# Revit family: Gas Ace 220_250_LOD-5
name_source: partatom
category: Mechanical Equipment
revit_build: Autodesk Revit 2015 (Build: 20160512_1515(x64)
units: mm (PartAtom-declared; Revit-internal decimal feet)

## types (1)
- 250
    6 Monthly = 0
    Access Clearance Bottom = 0.00 mm
    Access Clearance Front = 1100.00 mm
    Access Clearance Left = 100.00 mm
    Access Clearance Rear = 50.00 mm
    Access Clearance Right = 100.00 mm
    Access Clearance Top = 650.00 mm
    Additional Technical Details = https://www.remeha.co.uk
    Air Inlet Connection Size = 200.00 mm
    Annually = 0
    BMS Links = Yes
    Bespoke Timeframe = 0
    Building Regulations Seasonal Efficiency = 95.64 %
    Burner Control Type = Modulating
    CE Mark = 0063CQ3781
    Colour = RAL 2002 RAL 7016 Dark Grey
    Condensate Drain Size = 40.00 mm
    Condensate Drain Type = Plain
    Configuration = Single boiler
    Control Type = 0 - 10V, Open Therm, Volt free enable, Direct boiler weather compensating control systems available from Remeha as optional extra's.
    Daily = 0
    Drain Connection Size = 19.05 mm
    Drain Connection Type = Threaded
    Energy Technology List = 0
    ErP Energy Label = 0
    ErP Rated Efficiency at Full Load = 87.7 %
    ErP Rated Efficiency at Part Load = 97.5 %
    ErP Seasonal Efficiency = 0 %
    Expected Life = 15
    External Material = Steel
    Features = Remeha's Gas 220 Ace  is a compact high efficiency floor standing condensing boiler. The compact design make this boiler ideally suited to modular arrangements
    Finish = High Polish Gardner 60 GRAD 91EH
    Flow and Return Connection Size = 50.80 mm
    Flow and Return Connection Type = Threaded
    Flue Connection size = 200.00 mm
    Flue or Air Intake Classification = B23p,B33, C33, C43, C53, C63, C83, C89
    Frequency = 50 Hz
    Fuel Connection Size = 38.10 mm
    Fuel Connection Type = Threaded
    Full Load Current = 0 A
    Fuse Rating = 6 A
    Gas Consumption rate = 26.5 m3/h
    Gross Weight = 278.00 kg
    Heat Exchanger Material = Aluminium
    Heater Operation = Condensing
    Hydraulic Resistance at 11C temperature differential = 0.000
    Hydraulic Resistance at 20C temperature differential = 0.150
    IK Rating = 0
    IP Rating = IPX1B
    IfcExportAs = IfcBoilerType
    IfcExportType = NOTDEFINED
    Interlocks = Yes
    Maintenance Required 0 to 300hrs = 0
    Maintenance Required 1001 to 2000hrs = 0
    Maintenance Required 2001 to 4000hrs = 0
    Maintenance Required 301 to 600hrs = 0
    Maintenance Required 4001 to 8000hrs = 0
    Maintenance Required 601 to 1000hrs = 0
    Maintenance Required 8001 to 12000hrs = 0
    Manufacturer = Remeha Commercial
    Manufacturer Website = https://www.remeha.co.uk
    Maximum Gas Inlet Pressure = 0.025 bar
    Maximum Oil Inlet Pressure = 0.000 bar
    Maximum Operating Pressure = 5.000 bar
    Maximum Power Consumption = 323 W
    Minimum Flow Rate at 11C temperature differential = 0.0 L/s
    Minimum Flow Rate at 20C temperature differential = 2.9 L/s
    Minimum Gas Inlet Pressure = 0.017 bar
    Minimum Oil Inlet Pressure = 0.000 bar
    Minimum Operating Pressure = 0.800 bar
    Minimum Power Consumption = 11 W
    Monthly = 0
    Mounting = Floor Standing
    NOx Emissions = 38 mg/kWh
    Nominal Gas Inlet Pressure = 0.020 bar
    Nominal Oil Inlet Pressure = 0.000 bar
    Oil Consumption rate = 0
    Operation and Maintenance Manual = https://www.remeha.co.uk
    Optional Fuel = Gas - LPG
    Overall Height = 1662.00 mm
    Overall Length = 657.00 mm
    Overall Width = 800.00 mm
    Primary Fuel = Gas - NG
    Product Literature = https://www.remeha.co.uk
    Product Model Number = Not Available
    Product Range = Gas 220 -250
    Quarterly = 0
    Rated Criteria = 80/60
    Rated Output = 243300 W
    Reference Standard = GAD 2009/142/EC BED 92/42/EEC EMC 2014/35/EU LVD 2014/35/EU ErP 2009/125/EY
    Safety Valve Connection Size = 0.00 mm
    Safety Valve Connection Type = Unset
    Shape = Rectangular (Vertical)
    Shipping Weight = 275.00 kg
    Sound Pressure Level = 63.8 dBA
    Starting Current = 0 A
    Supply Phase = 1
    Turndown Ratio = 4.8:1
    Type = Space heating
    Uniclass2015 = Pr_60_60_08
    Voltage = 230 V
    Water Content = 33.0 L
    Water Treatment Required = Yes
    Weekly = 0

note: source unit labels omitted for Hydraulic Resistance at 11C temperature differential, Hydraulic Resistance at 20C temperature differential — the stored unit's dimension contradicts the parameter name (converter mislabeling)

## geometry (parser evidence)
native form markers: Blend x22, Sweep x2
no freeform markers — native parametric forms only
